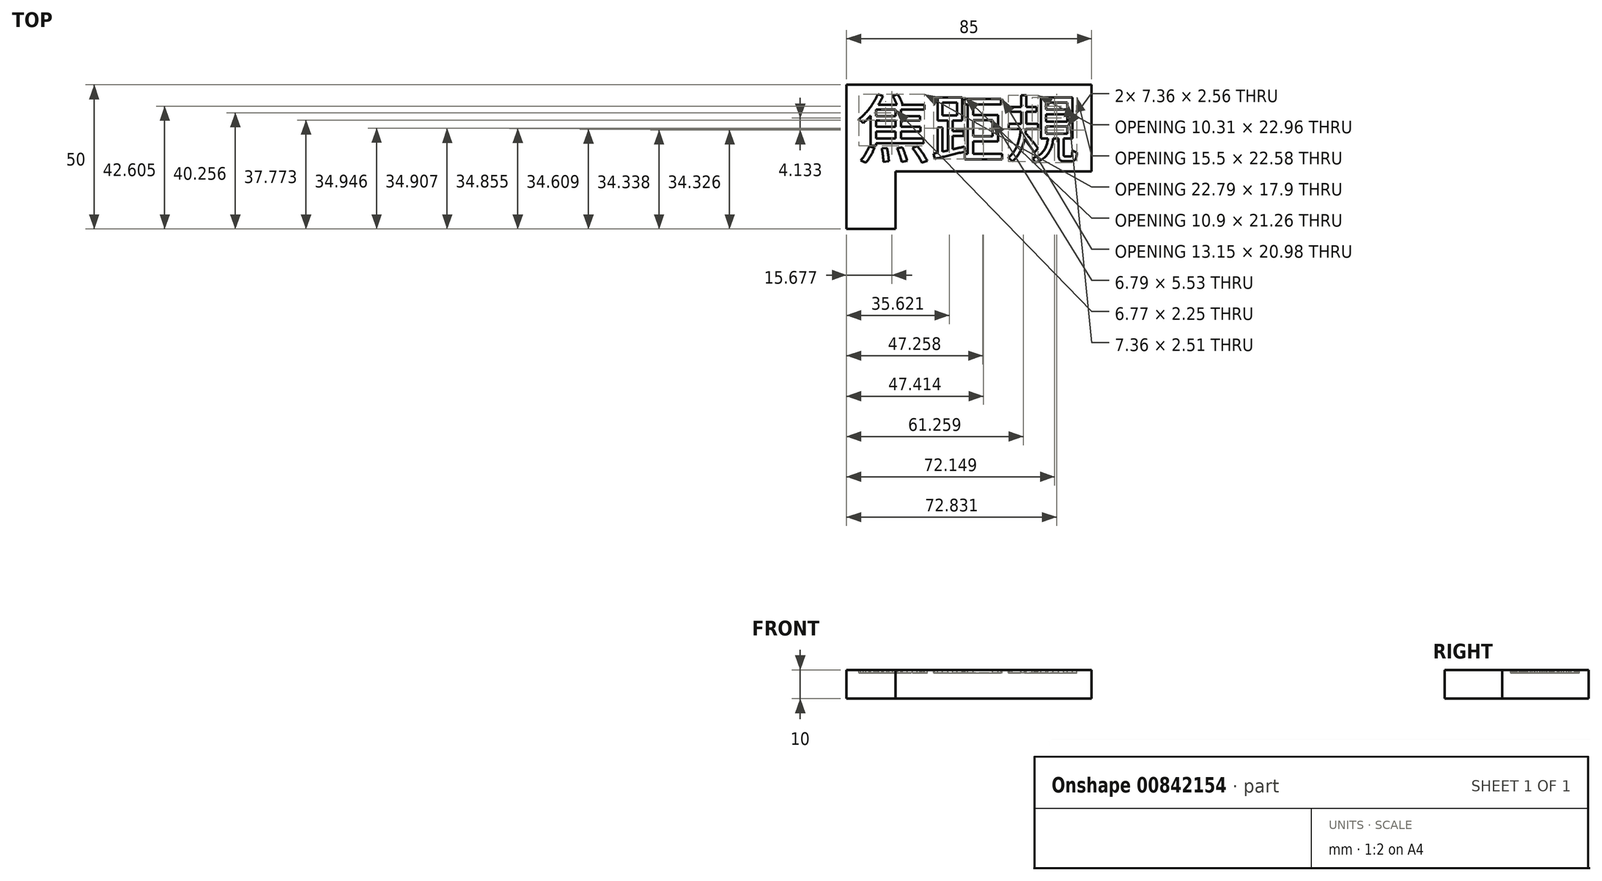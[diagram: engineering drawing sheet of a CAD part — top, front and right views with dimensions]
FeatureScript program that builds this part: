
annotation { "Feature Type Name" : "Feature", "Feature Type Description" : "" }
export const myFeature = defineFeature(function(context is Context, id is Id, definition is map)
    precondition{}
    {
        {
            var Q0;
            Q0=qCreatedBy(makeId("Top.planeOp"),FACE);
            var sketch = newSketch(context, id + "F0", { "sketchPlane" : qUnion([Q0])});
            skLineSegment(sketch, "E0.top", {"start": v(-42.5, 25) * mm, "end": v(42.5, 25) * mm});
            skLineSegment(sketch, "E0.left", {"start": v(-42.5, -25) * mm, "end": v(-42.5, 25) * mm});
            skLineSegment(sketch, "E0.right", {"start": v(42.5, -5) * mm, "end": v(42.5, 25) * mm});
            skPoint(sketch, "E0.middle", {"position": v(0, 0) * mm});
            skLineSegment(sketch, "E1", {"start": v(-42.5, -25) * mm, "end": v(-25.5, -25) * mm});
            skLineSegment(sketch, "E2", {"start": v(-25.5, -25) * mm, "end": v(-25.5, -5) * mm});
            skLineSegment(sketch, "E3", {"start": v(-25.5, -5) * mm, "end": v(42.5, -5) * mm});
            skPoint(sketch, "E4.orphan", {"position": v(42.5, -25) * mm});
            skSolve(sketch);
        }
        {
            var Q0;
            Q0 = qSketchRegion(id + "F0", true);
            extrude(context, id + "F1", {"entities" : qUnion([Q0]), "depth" : 10 * mm, "offsetDistance" : 25 * mm});
        }
        {
            var Q0;
            Q0=makeQuery(id+"F1.opExtrude","CAP_FACE",FACE,{"disambiguationData":[OSD([sQuery(id+"F0.wireOp",EDGE,"E0.top"),sQuery(id+"F0.wireOp",EDGE,"E0.left"),sQuery(id+"F0.wireOp",EDGE,"E0.right"),sQuery(id+"F0.wireOp",EDGE,"E1"),sQuery(id+"F0.wireOp",EDGE,"E2"),sQuery(id+"F0.wireOp",EDGE,"E3")])],"isStart":false});
            var sketch = newSketch(context, id + "F2", { "sketchPlane" : qUnion([Q0])});
            skText(sketch, "E5", { "text": "焦距規", "fontName": "NotoSansCJKtc-Regular.otf"});
            const initialGuessF2  = {"E5": [-0.03912, 0, 1, 0, 0.0186]};
            skSetInitialGuess(sketch, initialGuessF2);
            skSolve(sketch);
        }
        {
            var Q0;
            Q0 = qSketchRegion(id + "F2", true);
            extrude(context, id + "F3", {"entities" : qUnion([Q0]), "operationType" : NewBodyOperationType.REMOVE, "oppositeDirection" : true, "depth" : 1 * mm, "offsetDistance" : 25 * mm});
        }
    });
